annotation { "Feature Type Name" : "Feature", "Feature Type Description" : "" }
export const myFeature = defineFeature(function(context is Context, id is Id, definition is map)
    precondition{}
    {
        {
            var Q0;
            Q0=qCreatedBy(makeId("Front.planeOp"),FACE);
            var sketch = newSketch(context, id + "F0", { "sketchPlane" : qUnion([Q0])});
            skLineSegment(sketch, "E0", {"start": v(-50.37, 46.05) * mm, "end": v(25.9, 46.05) * mm});
            skLineSegment(sketch, "E1", {"start": v(25.9, 46.05) * mm, "end": v(25.9, -68.5) * mm});
            skLineSegment(sketch, "E2", {"start": v(25.9, -68.5) * mm, "end": v(-50.08, -68.5) * mm});
            skLineSegment(sketch, "E3", {"start": v(-50.08, -68.5) * mm, "end": v(-50.37, 46.05) * mm});
            skSolve(sketch);
        }
        {
            var Q0;
            Q0 = qSketchRegion(id + "F0", true);
            extrude(context, id + "F1", {"entities" : qUnion([Q0]), "depth" : 3.17 * mm});
        }
        {
            var Q0;
            Q0=makeQuery(id+"F1.opExtrude","CAP_FACE",FACE,{"disambiguationData":[OSD([sQuery(id+"F0.wireOp",EDGE,"E0"),sQuery(id+"F0.wireOp",EDGE,"E1"),sQuery(id+"F0.wireOp",EDGE,"E2"),sQuery(id+"F0.wireOp",EDGE,"E3")])],"isStart":false});
            var sketch = newSketch(context, id + "F2", { "sketchPlane" : qUnion([Q0])});
            skLineSegment(sketch, "E4", {"start": v(-31.14, 16.84) * mm, "end": v(-36.1, 15.38) * mm});
            skLineSegment(sketch, "E5", {"start": v(-36.1, 15.38) * mm, "end": v(-37.74, 17.03) * mm});
            skLineSegment(sketch, "E6", {"start": v(-37.74, 17.03) * mm, "end": v(-40.22, 17.03) * mm});
            skLineSegment(sketch, "E7", {"start": v(-40.22, 17.03) * mm, "end": v(-40.58, 17.03) * mm});
            skLineSegment(sketch, "E8", {"start": v(-40.58, 17.03) * mm, "end": v(-41.4, 15.93) * mm});
            skLineSegment(sketch, "E9", {"start": v(-41.4, 15.93) * mm, "end": v(-40.22, 15.03) * mm});
            skLineSegment(sketch, "E10", {"start": v(-40.33, 15.03) * mm, "end": v(-40.22, 15.03) * mm});
            skLineSegment(sketch, "E11", {"start": v(-40.33, 15.03) * mm, "end": v(-35.26, 13.62) * mm});
            skLineSegment(sketch, "E12", {"start": v(-35.26, 13.62) * mm, "end": v(-32.91, 12.55) * mm});
            skLineSegment(sketch, "E13", {"start": v(-32.91, 12.55) * mm, "end": v(-31.46, 11.23) * mm});
            skLineSegment(sketch, "E14", {"start": v(-31.46, 11.23) * mm, "end": v(-30.6, 8.92) * mm});
            skLineSegment(sketch, "E15", {"start": v(-30.6, 8.92) * mm, "end": v(-30.6, 6.47) * mm});
            skLineSegment(sketch, "E16", {"start": v(-30.6, 6.47) * mm, "end": v(-32.05, 4.3) * mm});
            skLineSegment(sketch, "E17", {"start": v(-32.05, 4.3) * mm, "end": v(-34.45, 2.44) * mm});
            skLineSegment(sketch, "E18", {"start": v(-34.45, 2.44) * mm, "end": v(-37.17, 1.8) * mm});
            skLineSegment(sketch, "E19", {"start": v(-37.17, 1.8) * mm, "end": v(-41.4, 1.8) * mm});
            skLineSegment(sketch, "E20", {"start": v(-41.4, 1.8) * mm, "end": v(-44.33, 2.7) * mm});
            skLineSegment(sketch, "E21", {"start": v(-44.33, 2.7) * mm, "end": v(-46.5, 4.34) * mm});
            skLineSegment(sketch, "E22", {"start": v(-46.5, 4.34) * mm, "end": v(-47.61, 6.19) * mm});
            skLineSegment(sketch, "E23", {"start": v(-47.61, 6.19) * mm, "end": v(-48.03, 7.19) * mm});
            skLineSegment(sketch, "E24", {"start": v(-48.03, 7.19) * mm, "end": v(-42.53, 8.2) * mm});
            skLineSegment(sketch, "E25", {"start": v(-42.53, 8.2) * mm, "end": v(-41.68, 7.01) * mm});
            skLineSegment(sketch, "E26", {"start": v(-41.68, 7.01) * mm, "end": v(-40.55, 6.32) * mm});
            skLineSegment(sketch, "E27", {"start": v(-40.55, 6.32) * mm, "end": v(-37.98, 6.32) * mm});
            skLineSegment(sketch, "E28", {"start": v(-37.98, 6.32) * mm, "end": v(-36.8, 6.69) * mm});
            skLineSegment(sketch, "E29", {"start": v(-36.8, 6.69) * mm, "end": v(-36.8, 7.66) * mm});
            skLineSegment(sketch, "E30", {"start": v(-36.8, 7.66) * mm, "end": v(-37.17, 8.34) * mm});
            skLineSegment(sketch, "E31", {"start": v(-37.17, 8.34) * mm, "end": v(-38.37, 8.73) * mm});
            skLineSegment(sketch, "E32", {"start": v(-38.37, 8.73) * mm, "end": v(-40.83, 9.23) * mm});
            skLineSegment(sketch, "E33", {"start": v(-40.83, 9.23) * mm, "end": v(-43.3, 9.95) * mm});
            skLineSegment(sketch, "E34", {"start": v(-43.3, 9.95) * mm, "end": v(-45.11, 10.93) * mm});
            skLineSegment(sketch, "E35", {"start": v(-45.11, 10.93) * mm, "end": v(-46.5, 12.51) * mm});
            skLineSegment(sketch, "E36", {"start": v(-46.5, 12.51) * mm, "end": v(-46.87, 13.9) * mm});
            skLineSegment(sketch, "E37", {"start": v(-46.87, 13.9) * mm, "end": v(-46.87, 15.38) * mm});
            skLineSegment(sketch, "E38", {"start": v(-46.87, 15.38) * mm, "end": v(-46.88, 17.03) * mm});
            skLineSegment(sketch, "E39", {"start": v(-46.88, 17.03) * mm, "end": v(-46.02, 18.57) * mm});
            skLineSegment(sketch, "E40", {"start": v(-46.02, 18.57) * mm, "end": v(-44.61, 20.07) * mm});
            skLineSegment(sketch, "E41", {"start": v(-44.61, 20.07) * mm, "end": v(-42.6, 21.17) * mm});
            skLineSegment(sketch, "E42", {"start": v(-42.6, 21.17) * mm, "end": v(-40.51, 21.54) * mm});
            skLineSegment(sketch, "E43", {"start": v(-40.51, 21.54) * mm, "end": v(-37.17, 21.54) * mm});
            skLineSegment(sketch, "E44", {"start": v(-37.17, 21.54) * mm, "end": v(-35.26, 21.04) * mm});
            skLineSegment(sketch, "E45", {"start": v(-35.26, 21.04) * mm, "end": v(-33.17, 19.89) * mm});
            skLineSegment(sketch, "E46", {"start": v(-33.17, 19.89) * mm, "end": v(-31.88, 18.39) * mm});
            skLineSegment(sketch, "E47", {"start": v(-31.88, 18.39) * mm, "end": v(-31.14, 16.84) * mm});
            skLineSegment(sketch, "E48", {"start": v(-29.85, 21.2) * mm, "end": v(-29.85, 16.84) * mm});
            skLineSegment(sketch, "E49", {"start": v(-29.85, 16.84) * mm, "end": v(-25.95, 16.84) * mm});
            skLineSegment(sketch, "E50", {"start": v(-25.95, 16.84) * mm, "end": v(-25.95, 2.18) * mm});
            skLineSegment(sketch, "E51", {"start": v(-25.95, 2.18) * mm, "end": v(-20.08, 2.18) * mm});
            skLineSegment(sketch, "E52", {"start": v(-20.08, 2.18) * mm, "end": v(-20.08, 16.84) * mm});
            skLineSegment(sketch, "E53", {"start": v(-20.08, 16.84) * mm, "end": v(-16.16, 16.84) * mm});
            skLineSegment(sketch, "E54", {"start": v(-16.16, 16.84) * mm, "end": v(-16.16, 21.26) * mm});
            skLineSegment(sketch, "E55", {"start": v(-16.16, 21.26) * mm, "end": v(-29.85, 21.2) * mm});
            skLineSegment(sketch, "E56", {"start": v(-14.65, 21.2) * mm, "end": v(-14.65, 2.18) * mm});
            skLineSegment(sketch, "E57", {"start": v(-14.65, 2.18) * mm, "end": v(0, 2.18) * mm});
            skLineSegment(sketch, "E58", {"start": v(0, 2.18) * mm, "end": v(0, 6.19) * mm});
            skLineSegment(sketch, "E59", {"start": v(0, 6.19) * mm, "end": v(-8.9, 6.19) * mm});
            skLineSegment(sketch, "E60", {"start": v(-8.9, 6.19) * mm, "end": v(-8.9, 9.7) * mm});
            skLineSegment(sketch, "E61", {"start": v(-8.9, 9.7) * mm, "end": v(-1.76, 9.7) * mm});
            skLineSegment(sketch, "E62", {"start": v(-1.76, 9.7) * mm, "end": v(-1.76, 14.12) * mm});
            skLineSegment(sketch, "E63", {"start": v(-1.76, 14.12) * mm, "end": v(-8.96, 14.12) * mm});
            skLineSegment(sketch, "E64", {"start": v(-8.96, 14.12) * mm, "end": v(-8.96, 16.84) * mm});
            skLineSegment(sketch, "E65", {"start": v(-8.96, 16.84) * mm, "end": v(0, 16.84) * mm});
            skLineSegment(sketch, "E66", {"start": v(0, 16.84) * mm, "end": v(0, 21.2) * mm});
            skLineSegment(sketch, "E67", {"start": v(0, 21.2) * mm, "end": v(-14.65, 21.2) * mm});
            skLineSegment(sketch, "E68", {"start": v(2.17, 21.2) * mm, "end": v(2.17, 2.01) * mm});
            skLineSegment(sketch, "E69", {"start": v(2.17, 2.01) * mm, "end": v(6.89, 2.01) * mm});
            skLineSegment(sketch, "E70", {"start": v(6.89, 2.01) * mm, "end": v(6.89, 15.02) * mm});
            skLineSegment(sketch, "E71", {"start": v(6.89, 15.02) * mm, "end": v(10.46, 1.95) * mm});
            skLineSegment(sketch, "E72", {"start": v(10.46, 1.95) * mm, "end": v(14.27, 1.95) * mm});
            skLineSegment(sketch, "E73", {"start": v(14.27, 1.95) * mm, "end": v(17.66, 15.2) * mm});
            skLineSegment(sketch, "E74", {"start": v(17.66, 15.2) * mm, "end": v(17.66, 1.83) * mm});
            skLineSegment(sketch, "E75", {"start": v(17.66, 1.83) * mm, "end": v(23.34, 1.83) * mm});
            skLineSegment(sketch, "E76", {"start": v(23.34, 1.83) * mm, "end": v(23.34, 21.2) * mm});
            skLineSegment(sketch, "E77", {"start": v(23.34, 21.2) * mm, "end": v(15.54, 21.2) * mm});
            skLineSegment(sketch, "E78", {"start": v(15.54, 21.2) * mm, "end": v(13, 11.57) * mm});
            skLineSegment(sketch, "E79", {"start": v(13, 11.57) * mm, "end": v(10.1, 21.2) * mm});
            skLineSegment(sketch, "E80", {"start": v(10.1, 21.2) * mm, "end": v(2.17, 21.2) * mm});
            skSolve(sketch);
        }
        {
            var Q0;
            Q0 = qSketchRegion(id + "F2", true);
            extrude(context, id + "F3", {"entities" : qUnion([Q0]), "operationType" : NewBodyOperationType.ADD, "depth" : 3.17 * mm});
        }
        {
            var Q0;
            Q0=makeQuery(id+"F1.opExtrude","CAP_FACE",FACE,{"disambiguationData":[OSD([sQuery(id+"F0.wireOp",EDGE,"E0"),sQuery(id+"F0.wireOp",EDGE,"E1"),sQuery(id+"F0.wireOp",EDGE,"E2"),sQuery(id+"F0.wireOp",EDGE,"E3")])],"isStart":false});
            var sketch = newSketch(context, id + "F4", { "sketchPlane" : qUnion([Q0])});
            skCircle(sketch, "E81", {"center": v(-13.1, 39.3) * mm, "radius": 3.65 * mm});
            skSolve(sketch);
        }
        {
            var Q0;
            Q0 = qSketchRegion(id + "F4", true);
            extrude(context, id + "F5", {"entities" : qUnion([Q0]), "operationType" : NewBodyOperationType.REMOVE, "oppositeDirection" : true, "depth" : 3.17 * mm});
        }
        {
            var Q0;
            Q0=makeQuery(id+"F1.opExtrude","CAP_FACE",FACE,{"disambiguationData":[OSD([sQuery(id+"F0.wireOp",EDGE,"E0"),sQuery(id+"F0.wireOp",EDGE,"E1"),sQuery(id+"F0.wireOp",EDGE,"E2"),sQuery(id+"F0.wireOp",EDGE,"E3")])],"isStart":false});
            var sketch = newSketch(context, id + "F6", { "sketchPlane" : qUnion([Q0])});
            skLineSegment(sketch, "E82", {"start": v(-41.83, -27.74) * mm, "end": v(-41.83, -28.28) * mm});
            skLineSegment(sketch, "E83", {"start": v(-41.83, -28.28) * mm, "end": v(-40.54, -28.73) * mm});
            skLineSegment(sketch, "E84", {"start": v(-40.54, -28.73) * mm, "end": v(-40.42, -35.14) * mm});
            skLineSegment(sketch, "E85", {"start": v(-40.42, -35.14) * mm, "end": v(-41.75, -35.75) * mm});
            skLineSegment(sketch, "E86", {"start": v(-41.75, -35.75) * mm, "end": v(-41.75, -36.27) * mm});
            skLineSegment(sketch, "E87", {"start": v(-41.75, -36.27) * mm, "end": v(-36.9, -36.27) * mm});
            skLineSegment(sketch, "E88", {"start": v(-36.9, -36.27) * mm, "end": v(-36.9, -35.75) * mm});
            skLineSegment(sketch, "E89", {"start": v(-36.9, -35.75) * mm, "end": v(-38, -35.32) * mm});
            skLineSegment(sketch, "E90", {"start": v(-38, -35.32) * mm, "end": v(-38, -32.36) * mm});
            skLineSegment(sketch, "E91", {"start": v(-38, -32.36) * mm, "end": v(-34.97, -36.12) * mm});
            skLineSegment(sketch, "E92", {"start": v(-34.97, -36.12) * mm, "end": v(-31.44, -36.24) * mm});
            skLineSegment(sketch, "E93", {"start": v(-31.44, -36.24) * mm, "end": v(-31.29, -35.75) * mm});
            skLineSegment(sketch, "E94", {"start": v(-31.29, -35.75) * mm, "end": v(-31.78, -35.74) * mm});
            skLineSegment(sketch, "E95", {"start": v(-31.78, -35.74) * mm, "end": v(-32.16, -35.52) * mm});
            skLineSegment(sketch, "E96", {"start": v(-32.16, -35.52) * mm, "end": v(-35.54, -32.08) * mm});
            skLineSegment(sketch, "E97", {"start": v(-35.54, -32.08) * mm, "end": v(-34.88, -31.86) * mm});
            skLineSegment(sketch, "E98", {"start": v(-34.88, -31.86) * mm, "end": v(-34.31, -31.4) * mm});
            skLineSegment(sketch, "E99", {"start": v(-34.31, -31.4) * mm, "end": v(-33.76, -30.87) * mm});
            skLineSegment(sketch, "E100", {"start": v(-33.76, -30.87) * mm, "end": v(-33.4, -30.07) * mm});
            skLineSegment(sketch, "E101", {"start": v(-33.4, -30.07) * mm, "end": v(-33.36, -29.25) * mm});
            skLineSegment(sketch, "E102", {"start": v(-33.36, -29.25) * mm, "end": v(-33.36, -28.73) * mm});
            skLineSegment(sketch, "E103", {"start": v(-33.36, -28.73) * mm, "end": v(-33.87, -28.34) * mm});
            skLineSegment(sketch, "E104", {"start": v(-33.87, -28.34) * mm, "end": v(-34.83, -27.77) * mm});
            skLineSegment(sketch, "E105", {"start": v(-34.83, -27.77) * mm, "end": v(-36.43, -27.5) * mm});
            skLineSegment(sketch, "E106", {"start": v(-36.43, -27.5) * mm, "end": v(-41.62, -27.5) * mm});
            skLineSegment(sketch, "E107", {"start": v(-41.62, -27.5) * mm, "end": v(-41.83, -27.5) * mm});
            skLineSegment(sketch, "E108", {"start": v(-41.83, -27.5) * mm, "end": v(-41.83, -27.74) * mm});
            skLineSegment(sketch, "E109", {"start": v(-38.26, -28.2) * mm, "end": v(-38.26, -31.44) * mm});
            skLineSegment(sketch, "E110", {"start": v(-38.26, -31.44) * mm, "end": v(-38.04, -31.61) * mm});
            skLineSegment(sketch, "E111", {"start": v(-38.04, -31.61) * mm, "end": v(-37.21, -31.44) * mm});
            skLineSegment(sketch, "E112", {"start": v(-37.21, -31.44) * mm, "end": v(-36.5, -30.94) * mm});
            skLineSegment(sketch, "E113", {"start": v(-36.5, -30.94) * mm, "end": v(-36.13, -30.4) * mm});
            skLineSegment(sketch, "E114", {"start": v(-36.13, -30.4) * mm, "end": v(-36.13, -29.81) * mm});
            skLineSegment(sketch, "E115", {"start": v(-36.13, -29.81) * mm, "end": v(-36.13, -29.16) * mm});
            skLineSegment(sketch, "E116", {"start": v(-36.13, -29.16) * mm, "end": v(-36.37, -28.73) * mm});
            skLineSegment(sketch, "E117", {"start": v(-36.37, -28.73) * mm, "end": v(-36.95, -28.36) * mm});
            skLineSegment(sketch, "E118", {"start": v(-36.95, -28.36) * mm, "end": v(-37.67, -28.18) * mm});
            skLineSegment(sketch, "E119", {"start": v(-37.67, -28.18) * mm, "end": v(-38.26, -28.2) * mm});
            skLineSegment(sketch, "E120", {"start": v(-27.32, -32.37) * mm, "end": v(-27.64, -31.1) * mm});
            skLineSegment(sketch, "E121", {"start": v(-27.64, -31.1) * mm, "end": v(-27.82, -30.75) * mm});
            skLineSegment(sketch, "E122", {"start": v(-27.82, -30.75) * mm, "end": v(-28.05, -30.66) * mm});
            skLineSegment(sketch, "E123", {"start": v(-28.05, -30.66) * mm, "end": v(-28.33, -30.66) * mm});
            skLineSegment(sketch, "E124", {"start": v(-28.33, -30.66) * mm, "end": v(-28.66, -30.8) * mm});
            skLineSegment(sketch, "E125", {"start": v(-28.66, -30.8) * mm, "end": v(-28.95, -31.11) * mm});
            skLineSegment(sketch, "E126", {"start": v(-28.95, -31.11) * mm, "end": v(-29.16, -31.66) * mm});
            skLineSegment(sketch, "E127", {"start": v(-29.16, -31.66) * mm, "end": v(-29.23, -32.46) * mm});
            skLineSegment(sketch, "E128", {"start": v(-29.23, -32.46) * mm, "end": v(-27.32, -32.37) * mm});
            skLineSegment(sketch, "E129", {"start": v(-24.94, -33.17) * mm, "end": v(-24.94, -32.53) * mm});
            skLineSegment(sketch, "E130", {"start": v(-24.94, -32.53) * mm, "end": v(-25.27, -31.66) * mm});
            skLineSegment(sketch, "E131", {"start": v(-25.27, -31.66) * mm, "end": v(-25.6, -31.05) * mm});
            skLineSegment(sketch, "E132", {"start": v(-25.6, -31.05) * mm, "end": v(-26.56, -30.34) * mm});
            skLineSegment(sketch, "E133", {"start": v(-26.56, -30.34) * mm, "end": v(-27.98, -29.93) * mm});
            skLineSegment(sketch, "E134", {"start": v(-27.98, -29.93) * mm, "end": v(-28.86, -29.93) * mm});
            skLineSegment(sketch, "E135", {"start": v(-28.86, -29.93) * mm, "end": v(-29.65, -30.29) * mm});
            skLineSegment(sketch, "E136", {"start": v(-29.65, -30.29) * mm, "end": v(-30.78, -31.22) * mm});
            skLineSegment(sketch, "E137", {"start": v(-30.78, -31.22) * mm, "end": v(-31.3, -32.18) * mm});
            skLineSegment(sketch, "E138", {"start": v(-31.3, -32.18) * mm, "end": v(-31.3, -32.68) * mm});
            skLineSegment(sketch, "E139", {"start": v(-31.3, -32.68) * mm, "end": v(-31.3, -34.6) * mm});
            skLineSegment(sketch, "E140", {"start": v(-31.3, -34.6) * mm, "end": v(-30.68, -35.6) * mm});
            skLineSegment(sketch, "E141", {"start": v(-30.68, -35.6) * mm, "end": v(-29.27, -36.5) * mm});
            skLineSegment(sketch, "E142", {"start": v(-29.27, -36.5) * mm, "end": v(-26.97, -36.5) * mm});
            skLineSegment(sketch, "E143", {"start": v(-26.97, -36.5) * mm, "end": v(-25.5, -35.6) * mm});
            skLineSegment(sketch, "E144", {"start": v(-25.5, -35.6) * mm, "end": v(-24.83, -34.85) * mm});
            skLineSegment(sketch, "E145", {"start": v(-24.83, -34.85) * mm, "end": v(-25.22, -34.5) * mm});
            skLineSegment(sketch, "E146", {"start": v(-25.22, -34.5) * mm, "end": v(-25.87, -35.22) * mm});
            skLineSegment(sketch, "E147", {"start": v(-25.87, -35.22) * mm, "end": v(-27.43, -35.6) * mm});
            skLineSegment(sketch, "E148", {"start": v(-27.43, -35.6) * mm, "end": v(-28.62, -35.15) * mm});
            skLineSegment(sketch, "E149", {"start": v(-28.62, -35.15) * mm, "end": v(-29.28, -34.26) * mm});
            skLineSegment(sketch, "E150", {"start": v(-29.28, -34.26) * mm, "end": v(-29.28, -33.15) * mm});
            skLineSegment(sketch, "E151", {"start": v(-29.28, -33.15) * mm, "end": v(-24.94, -33.17) * mm});
            skLineSegment(sketch, "E152", {"start": v(-18.59, -34.42) * mm, "end": v(-18.1, -34.75) * mm});
            skLineSegment(sketch, "E153", {"start": v(-18.1, -34.75) * mm, "end": v(-18.65, -35.57) * mm});
            skLineSegment(sketch, "E154", {"start": v(-18.65, -35.57) * mm, "end": v(-20.04, -36.4) * mm});
            skLineSegment(sketch, "E155", {"start": v(-20.04, -36.4) * mm, "end": v(-22.5, -36.4) * mm});
            skLineSegment(sketch, "E156", {"start": v(-22.5, -36.4) * mm, "end": v(-23.81, -35.25) * mm});
            skLineSegment(sketch, "E157", {"start": v(-23.81, -35.25) * mm, "end": v(-24.2, -34.7) * mm});
            skLineSegment(sketch, "E158", {"start": v(-24.2, -34.7) * mm, "end": v(-24.4, -34.23) * mm});
            skLineSegment(sketch, "E159", {"start": v(-24.4, -34.23) * mm, "end": v(-24.4, -33.25) * mm});
            skLineSegment(sketch, "E160", {"start": v(-24.4, -33.25) * mm, "end": v(-24, -32.01) * mm});
            skLineSegment(sketch, "E161", {"start": v(-24, -32.01) * mm, "end": v(-23.08, -30.81) * mm});
            skLineSegment(sketch, "E162", {"start": v(-23.08, -30.81) * mm, "end": v(-21.67, -30.18) * mm});
            skLineSegment(sketch, "E163", {"start": v(-21.67, -30.18) * mm, "end": v(-21.14, -29.93) * mm});
            skLineSegment(sketch, "E164", {"start": v(-21.14, -29.93) * mm, "end": v(-20.16, -29.93) * mm});
            skLineSegment(sketch, "E165", {"start": v(-20.16, -29.93) * mm, "end": v(-19.14, -30.44) * mm});
            skLineSegment(sketch, "E166", {"start": v(-19.14, -30.44) * mm, "end": v(-18.62, -30.76) * mm});
            skLineSegment(sketch, "E167", {"start": v(-18.62, -30.76) * mm, "end": v(-18.37, -31.15) * mm});
            skLineSegment(sketch, "E168", {"start": v(-18.37, -31.15) * mm, "end": v(-18.37, -31.83) * mm});
            skLineSegment(sketch, "E169", {"start": v(-18.37, -31.83) * mm, "end": v(-18.63, -32.27) * mm});
            skLineSegment(sketch, "E170", {"start": v(-18.63, -32.27) * mm, "end": v(-19.07, -32.62) * mm});
            skLineSegment(sketch, "E171", {"start": v(-19.07, -32.62) * mm, "end": v(-19.63, -32.62) * mm});
            skLineSegment(sketch, "E172", {"start": v(-19.63, -32.62) * mm, "end": v(-20.23, -32.34) * mm});
            skLineSegment(sketch, "E173", {"start": v(-20.23, -32.34) * mm, "end": v(-20.55, -32.03) * mm});
            skLineSegment(sketch, "E174", {"start": v(-20.55, -32.03) * mm, "end": v(-20.55, -31.54) * mm});
            skLineSegment(sketch, "E175", {"start": v(-20.55, -31.54) * mm, "end": v(-20.3, -31.01) * mm});
            skLineSegment(sketch, "E176", {"start": v(-20.3, -31.01) * mm, "end": v(-20.3, -30.78) * mm});
            skLineSegment(sketch, "E177", {"start": v(-20.3, -30.78) * mm, "end": v(-20.89, -30.67) * mm});
            skLineSegment(sketch, "E178", {"start": v(-20.89, -30.67) * mm, "end": v(-21.42, -30.82) * mm});
            skLineSegment(sketch, "E179", {"start": v(-21.42, -30.82) * mm, "end": v(-22.02, -31.55) * mm});
            skLineSegment(sketch, "E180", {"start": v(-22.02, -31.55) * mm, "end": v(-22.31, -32.52) * mm});
            skLineSegment(sketch, "E181", {"start": v(-22.31, -32.52) * mm, "end": v(-22.31, -33.84) * mm});
            skLineSegment(sketch, "E182", {"start": v(-22.31, -33.84) * mm, "end": v(-21.44, -35.14) * mm});
            skLineSegment(sketch, "E183", {"start": v(-21.44, -35.14) * mm, "end": v(-20.37, -35.45) * mm});
            skLineSegment(sketch, "E184", {"start": v(-20.37, -35.45) * mm, "end": v(-19.58, -35.45) * mm});
            skLineSegment(sketch, "E185", {"start": v(-19.58, -35.45) * mm, "end": v(-18.93, -34.92) * mm});
            skLineSegment(sketch, "E186", {"start": v(-15.88, -37.9) * mm, "end": v(-15.88, -37.67) * mm});
            skLineSegment(sketch, "E187", {"start": v(-15.88, -37.67) * mm, "end": v(-16.3, -37.2) * mm});
            skLineSegment(sketch, "E188", {"start": v(-16.3, -37.2) * mm, "end": v(-16.77, -36.96) * mm});
            skLineSegment(sketch, "E189", {"start": v(-16.77, -36.96) * mm, "end": v(-17.29, -36.96) * mm});
            skLineSegment(sketch, "E190", {"start": v(-17.29, -36.96) * mm, "end": v(-17.96, -37.39) * mm});
            skLineSegment(sketch, "E191", {"start": v(-17.96, -37.39) * mm, "end": v(-18.24, -37.78) * mm});
            skLineSegment(sketch, "E192", {"start": v(-18.24, -37.78) * mm, "end": v(-18.24, -38.34) * mm});
            skLineSegment(sketch, "E193", {"start": v(-18.24, -38.34) * mm, "end": v(-17.76, -38.88) * mm});
            skLineSegment(sketch, "E194", {"start": v(-17.76, -38.88) * mm, "end": v(-17.4, -39.17) * mm});
            skLineSegment(sketch, "E195", {"start": v(-17.4, -39.17) * mm, "end": v(-16.4, -39.17) * mm});
            skLineSegment(sketch, "E196", {"start": v(-16.4, -39.17) * mm, "end": v(-15.55, -38.64) * mm});
            skLineSegment(sketch, "E197", {"start": v(-15.55, -38.64) * mm, "end": v(-15.11, -38.3) * mm});
            skLineSegment(sketch, "E198", {"start": v(-15.11, -38.3) * mm, "end": v(-14.13, -36.27) * mm});
            skLineSegment(sketch, "E199", {"start": v(-14.13, -36.27) * mm, "end": v(-11.5, -30.83) * mm});
            skLineSegment(sketch, "E200", {"start": v(-11.5, -30.83) * mm, "end": v(-10.93, -30.57) * mm});
            skLineSegment(sketch, "E201", {"start": v(-10.93, -30.57) * mm, "end": v(-10.93, -30.25) * mm});
            skLineSegment(sketch, "E202", {"start": v(-10.93, -30.25) * mm, "end": v(-13.58, -30.25) * mm});
            skLineSegment(sketch, "E203", {"start": v(-13.58, -30.25) * mm, "end": v(-13.58, -30.78) * mm});
            skLineSegment(sketch, "E204", {"start": v(-13.58, -30.78) * mm, "end": v(-13.58, -31.04) * mm});
            skLineSegment(sketch, "E205", {"start": v(-13.58, -31.04) * mm, "end": v(-12.8, -31.04) * mm});
            skLineSegment(sketch, "E206", {"start": v(-12.8, -31.04) * mm, "end": v(-12.54, -31.04) * mm});
            skLineSegment(sketch, "E207", {"start": v(-12.54, -31.04) * mm, "end": v(-13.97, -34.32) * mm});
            skLineSegment(sketch, "E208", {"start": v(-13.97, -34.32) * mm, "end": v(-15.6, -31.08) * mm});
            skLineSegment(sketch, "E209", {"start": v(-15.6, -31.08) * mm, "end": v(-14.91, -30.4) * mm});
            skLineSegment(sketch, "E210", {"start": v(-14.91, -30.4) * mm, "end": v(-16.47, -30.4) * mm});
            skLineSegment(sketch, "E211", {"start": v(-16.47, -30.4) * mm, "end": v(-18.53, -30.4) * mm});
            skLineSegment(sketch, "E212", {"start": v(-18.53, -30.4) * mm, "end": v(-18.26, -31.1) * mm});
            skLineSegment(sketch, "E213", {"start": v(-18.26, -31.1) * mm, "end": v(-17.86, -31.1) * mm});
            skLineSegment(sketch, "E214", {"start": v(-17.86, -31.1) * mm, "end": v(-15.92, -34.49) * mm});
            skLineSegment(sketch, "E215", {"start": v(-15.92, -34.49) * mm, "end": v(-14.86, -36.37) * mm});
            skLineSegment(sketch, "E216", {"start": v(-10.54, -33.8) * mm, "end": v(-10.1, -34.97) * mm});
            skLineSegment(sketch, "E217", {"start": v(-10.1, -34.97) * mm, "end": v(-9.21, -36.02) * mm});
            skLineSegment(sketch, "E218", {"start": v(-9.21, -36.02) * mm, "end": v(-7.8, -36.42) * mm});
            skLineSegment(sketch, "E219", {"start": v(-7.8, -36.42) * mm, "end": v(-6.52, -36.42) * mm});
            skLineSegment(sketch, "E220", {"start": v(-6.52, -36.42) * mm, "end": v(-5.74, -36.17) * mm});
            skLineSegment(sketch, "E221", {"start": v(-5.74, -36.17) * mm, "end": v(-4.75, -35.48) * mm});
            skLineSegment(sketch, "E222", {"start": v(-4.75, -35.48) * mm, "end": v(-4.08, -34.65) * mm});
            skLineSegment(sketch, "E223", {"start": v(-4.08, -34.65) * mm, "end": v(-4.42, -34.38) * mm});
            skPoint(sketch, "E223.endSnap0", {"position": v(-4.42, -35.07) * mm});
            skLineSegment(sketch, "E224", {"start": v(-4.42, -34.38) * mm, "end": v(-5.48, -35.26) * mm});
            skLineSegment(sketch, "E225", {"start": v(-5.48, -35.26) * mm, "end": v(-6.35, -35.52) * mm});
            skLineSegment(sketch, "E226", {"start": v(-6.35, -35.52) * mm, "end": v(-7.32, -35.24) * mm});
            skLineSegment(sketch, "E227", {"start": v(-7.32, -35.24) * mm, "end": v(-7.77, -34.84) * mm});
            skLineSegment(sketch, "E228", {"start": v(-7.77, -34.84) * mm, "end": v(-8.35, -33.86) * mm});
            skLineSegment(sketch, "E229", {"start": v(-8.35, -33.86) * mm, "end": v(-8.35, -32.16) * mm});
            skLineSegment(sketch, "E230", {"start": v(-8.35, -32.16) * mm, "end": v(-7.87, -31.19) * mm});
            skLineSegment(sketch, "E231", {"start": v(-7.87, -31.19) * mm, "end": v(-7.17, -30.68) * mm});
            skLineSegment(sketch, "E232", {"start": v(-7.17, -30.68) * mm, "end": v(-6.38, -30.68) * mm});
            skLineSegment(sketch, "E233", {"start": v(-6.38, -30.68) * mm, "end": v(-6.08, -31) * mm});
            skLineSegment(sketch, "E234", {"start": v(-6.08, -31) * mm, "end": v(-6.48, -31) * mm});
            skLineSegment(sketch, "E235", {"start": v(-6.48, -31) * mm, "end": v(-6.74, -31.78) * mm});
            skLineSegment(sketch, "E236", {"start": v(-6.74, -31.78) * mm, "end": v(-6.44, -32.59) * mm});
            skLineSegment(sketch, "E237", {"start": v(-6.44, -32.59) * mm, "end": v(-5.41, -32.9) * mm});
            skLineSegment(sketch, "E238", {"start": v(-5.41, -32.9) * mm, "end": v(-4.66, -32.42) * mm});
            skLineSegment(sketch, "E239", {"start": v(-4.66, -32.42) * mm, "end": v(-4.66, -31.45) * mm});
            skLineSegment(sketch, "E240", {"start": v(-4.66, -31.45) * mm, "end": v(-4.66, -30.82) * mm});
            skLineSegment(sketch, "E241", {"start": v(-4.66, -30.82) * mm, "end": v(-5.51, -30.27) * mm});
            skLineSegment(sketch, "E242", {"start": v(-5.51, -30.27) * mm, "end": v(-6.55, -29.91) * mm});
            skLineSegment(sketch, "E243", {"start": v(-6.55, -29.91) * mm, "end": v(-7.52, -29.91) * mm});
            skPoint(sketch, "E243.endSnap0", {"position": v(-7.52, -30.93) * mm});
            skLineSegment(sketch, "E244", {"start": v(-7.52, -29.91) * mm, "end": v(-8.78, -30.45) * mm});
            skLineSegment(sketch, "E245", {"start": v(-8.78, -30.45) * mm, "end": v(-9.88, -31.4) * mm});
            skLineSegment(sketch, "E246", {"start": v(-9.88, -31.4) * mm, "end": v(-10.54, -32.5) * mm});
            skLineSegment(sketch, "E247", {"start": v(-10.54, -32.5) * mm, "end": v(-10.54, -33.8) * mm});
            skLineSegment(sketch, "E248", {"start": v(-3.53, -27.77) * mm, "end": v(-4.66, -27.77) * mm});
            skLineSegment(sketch, "E249", {"start": v(-4.66, -27.77) * mm, "end": v(-4.66, -26.8) * mm});
            skLineSegment(sketch, "E250", {"start": v(-4.66, -26.8) * mm, "end": v(-1.43, -26.8) * mm});
            skLineSegment(sketch, "E251", {"start": v(-1.43, -26.8) * mm, "end": v(-1.43, -35.44) * mm});
            skLineSegment(sketch, "E252", {"start": v(-1.43, -35.44) * mm, "end": v(-0.36, -35.82) * mm});
            skLineSegment(sketch, "E253", {"start": v(-0.36, -35.82) * mm, "end": v(-0.36, -36.4) * mm});
            skLineSegment(sketch, "E254", {"start": v(-0.36, -36.4) * mm, "end": v(-4.51, -36.4) * mm});
            skLineSegment(sketch, "E255", {"start": v(-4.51, -36.4) * mm, "end": v(-4.42, -35.9) * mm});
            skLineSegment(sketch, "E256", {"start": v(-4.42, -35.9) * mm, "end": v(-3.44, -35.44) * mm});
            skLineSegment(sketch, "E257", {"start": v(-3.44, -35.44) * mm, "end": v(-3.44, -33.2) * mm});
            skLineSegment(sketch, "E258", {"start": v(-3.44, -33.2) * mm, "end": v(-3.53, -27.77) * mm});
            skLineSegment(sketch, "E259", {"start": v(2.54, -30) * mm, "end": v(2.54, -35.48) * mm});
            skLineSegment(sketch, "E260", {"start": v(2.54, -35.48) * mm, "end": v(3.64, -35.92) * mm});
            skLineSegment(sketch, "E261", {"start": v(3.64, -35.92) * mm, "end": v(3.64, -36.24) * mm});
            skLineSegment(sketch, "E262", {"start": v(3.64, -36.24) * mm, "end": v(0, -36.24) * mm});
            skLineSegment(sketch, "E263", {"start": v(0, -36.24) * mm, "end": v(-0.36, -36.11) * mm});
            skLineSegment(sketch, "E264", {"start": v(-0.36, -36.11) * mm, "end": v(-0.36, -35.82) * mm});
            skLineSegment(sketch, "E265", {"start": v(0, -35.7) * mm, "end": v(-0.36, -35.82) * mm});
            skLineSegment(sketch, "E266", {"start": v(0.44, -35.64) * mm, "end": v(0, -35.7) * mm});
            skLineSegment(sketch, "E267", {"start": v(0.44, -35.64) * mm, "end": v(0.44, -31.16) * mm});
            skLineSegment(sketch, "E268", {"start": v(0.44, -31.16) * mm, "end": v(-0.8, -30.8) * mm});
            skLineSegment(sketch, "E269", {"start": v(-0.8, -30.8) * mm, "end": v(-0.65, -30.28) * mm});
            skLineSegment(sketch, "E270", {"start": v(-0.65, -30.28) * mm, "end": v(1.86, -30.16) * mm});
            skLineSegment(sketch, "E271", {"start": v(1.86, -30.16) * mm, "end": v(2.54, -30) * mm});
            skLineSegment(sketch, "E272", {"start": v(4.44, -30.95) * mm, "end": v(4.44, -35.81) * mm});
            skLineSegment(sketch, "E273", {"start": v(4.44, -35.81) * mm, "end": v(3.64, -35.92) * mm});
            skLineSegment(sketch, "E274", {"start": v(3.62, -36.34) * mm, "end": v(7.34, -36.34) * mm});
            skLineSegment(sketch, "E275", {"start": v(7.34, -36.34) * mm, "end": v(7.34, -35.78) * mm});
            skLineSegment(sketch, "E276", {"start": v(7.34, -35.78) * mm, "end": v(6.4, -35.78) * mm});
            skLineSegment(sketch, "E277", {"start": v(6.4, -35.78) * mm, "end": v(6.4, -31.87) * mm});
            skLineSegment(sketch, "E278", {"start": v(6.4, -31.87) * mm, "end": v(7.24, -31.33) * mm});
            skLineSegment(sketch, "E279", {"start": v(7.24, -31.33) * mm, "end": v(7.94, -31.33) * mm});
            skLineSegment(sketch, "E280", {"start": v(7.94, -31.33) * mm, "end": v(8.8, -31.89) * mm});
            skLineSegment(sketch, "E281", {"start": v(8.8, -31.89) * mm, "end": v(8.8, -35.76) * mm});
            skLineSegment(sketch, "E282", {"start": v(8.8, -35.76) * mm, "end": v(8.05, -35.76) * mm});
            skLineSegment(sketch, "E283", {"start": v(8.05, -35.76) * mm, "end": v(8.05, -36.38) * mm});
            skLineSegment(sketch, "E284", {"start": v(8.05, -36.38) * mm, "end": v(11.97, -36.38) * mm});
            skLineSegment(sketch, "E285", {"start": v(11.97, -36.38) * mm, "end": v(11.97, -35.73) * mm});
            skLineSegment(sketch, "E286", {"start": v(11.97, -35.73) * mm, "end": v(10.95, -35.73) * mm});
            skLineSegment(sketch, "E287", {"start": v(10.95, -35.73) * mm, "end": v(10.95, -31.26) * mm});
            skLineSegment(sketch, "E288", {"start": v(10.95, -31.26) * mm, "end": v(10.08, -30.21) * mm});
            skLineSegment(sketch, "E289", {"start": v(10.08, -30.21) * mm, "end": v(8.8, -30.21) * mm});
            skLineSegment(sketch, "E290", {"start": v(8.8, -30.21) * mm, "end": v(8, -30.21) * mm});
            skLineSegment(sketch, "E291", {"start": v(8, -30.21) * mm, "end": v(6.66, -30.93) * mm});
            skLineSegment(sketch, "E292", {"start": v(6.66, -30.93) * mm, "end": v(6.66, -30.07) * mm});
            skLineSegment(sketch, "E293", {"start": v(6.66, -30.07) * mm, "end": v(3.4, -30.07) * mm});
            skLineSegment(sketch, "E294", {"start": v(3.4, -30.07) * mm, "end": v(3.4, -30.84) * mm});
            skLineSegment(sketch, "E295", {"start": v(3.64, -36.24) * mm, "end": v(7.34, -36.34) * mm});
            skLineSegment(sketch, "E296", {"start": v(19.01, -30.28) * mm, "end": v(18.92, -31.1) * mm});
            skLineSegment(sketch, "E297", {"start": v(18.92, -31.1) * mm, "end": v(17.66, -31.06) * mm});
            skLineSegment(sketch, "E298", {"start": v(17.66, -31.06) * mm, "end": v(18, -32.19) * mm});
            skLineSegment(sketch, "E299", {"start": v(18, -32.19) * mm, "end": v(17.5, -32.93) * mm});
            skLineSegment(sketch, "E300", {"start": v(17.5, -32.93) * mm, "end": v(16.92, -33.58) * mm});
            skLineSegment(sketch, "E301", {"start": v(16.92, -33.58) * mm, "end": v(15.32, -34.13) * mm});
            skLineSegment(sketch, "E302", {"start": v(15.32, -34.13) * mm, "end": v(14.32, -34.13) * mm});
            skLineSegment(sketch, "E303", {"start": v(14.32, -34.13) * mm, "end": v(13.77, -34.48) * mm});
            skLineSegment(sketch, "E304", {"start": v(13.77, -34.48) * mm, "end": v(14, -34.84) * mm});
            skLineSegment(sketch, "E305", {"start": v(14, -34.84) * mm, "end": v(17.66, -34.84) * mm});
            skLineSegment(sketch, "E306", {"start": v(17.66, -34.84) * mm, "end": v(18.48, -35.5) * mm});
            skLineSegment(sketch, "E307", {"start": v(18.48, -35.5) * mm, "end": v(18.87, -36.56) * mm});
            skLineSegment(sketch, "E308", {"start": v(18.87, -36.56) * mm, "end": v(18.65, -37.85) * mm});
            skLineSegment(sketch, "E309", {"start": v(18.65, -37.85) * mm, "end": v(16.83, -38.91) * mm});
            skLineSegment(sketch, "E310", {"start": v(16.83, -38.91) * mm, "end": v(13.28, -38.91) * mm});
            skLineSegment(sketch, "E311", {"start": v(13.28, -38.91) * mm, "end": v(12.7, -38.91) * mm});
            skLineSegment(sketch, "E312", {"start": v(12.7, -38.91) * mm, "end": v(12.1, -38.56) * mm});
            skLineSegment(sketch, "E313", {"start": v(12.1, -38.56) * mm, "end": v(11.8, -38.1) * mm});
            skLineSegment(sketch, "E314", {"start": v(11.8, -38.1) * mm, "end": v(11.8, -37.53) * mm});
            skLineSegment(sketch, "E315", {"start": v(11.8, -37.53) * mm, "end": v(11.98, -36.96) * mm});
            skLineSegment(sketch, "E316", {"start": v(11.98, -36.96) * mm, "end": v(13.4, -36.39) * mm});
            skLineSegment(sketch, "E317", {"start": v(13.4, -36.39) * mm, "end": v(12.6, -35.73) * mm});
            skLineSegment(sketch, "E318", {"start": v(12.6, -35.73) * mm, "end": v(12.25, -34.94) * mm});
            skLineSegment(sketch, "E319", {"start": v(12.25, -34.94) * mm, "end": v(13.02, -34.32) * mm});
            skLineSegment(sketch, "E320", {"start": v(13.02, -34.32) * mm, "end": v(13.77, -34.07) * mm});
            skLineSegment(sketch, "E321", {"start": v(13.77, -34.07) * mm, "end": v(12.53, -33.42) * mm});
            skLineSegment(sketch, "E322", {"start": v(12.53, -33.42) * mm, "end": v(12.07, -32.68) * mm});
            skLineSegment(sketch, "E323", {"start": v(12.07, -32.68) * mm, "end": v(12.07, -31.82) * mm});
            skLineSegment(sketch, "E324", {"start": v(12.07, -31.82) * mm, "end": v(12.18, -31.08) * mm});
            skLineSegment(sketch, "E325", {"start": v(12.18, -31.08) * mm, "end": v(13.18, -30.37) * mm});
            skLineSegment(sketch, "E326", {"start": v(13.18, -30.37) * mm, "end": v(14.4, -30.09) * mm});
            skLineSegment(sketch, "E327", {"start": v(14.4, -30.09) * mm, "end": v(15.7, -30.15) * mm});
            skLineSegment(sketch, "E328", {"start": v(15.7, -30.15) * mm, "end": v(16.21, -30.49) * mm});
            skLineSegment(sketch, "E329", {"start": v(16.21, -30.49) * mm, "end": v(19.01, -30.28) * mm});
            skLineSegment(sketch, "E330", {"start": v(14.91, -30.67) * mm, "end": v(15.44, -31.03) * mm});
            skLineSegment(sketch, "E331", {"start": v(15.44, -31.03) * mm, "end": v(15.85, -31.37) * mm});
            skLineSegment(sketch, "E332", {"start": v(15.85, -31.37) * mm, "end": v(15.32, -33.53) * mm});
            skLineSegment(sketch, "E333", {"start": v(15.32, -33.53) * mm, "end": v(14.83, -33.53) * mm});
            skLineSegment(sketch, "E334", {"start": v(14.83, -33.53) * mm, "end": v(14.32, -33.17) * mm});
            skLineSegment(sketch, "E335", {"start": v(14.32, -33.17) * mm, "end": v(14.32, -31.32) * mm});
            skLineSegment(sketch, "E336", {"start": v(14.32, -31.32) * mm, "end": v(14.44, -30.86) * mm});
            skLineSegment(sketch, "E337", {"start": v(14.44, -30.86) * mm, "end": v(14.91, -30.67) * mm});
            skLineSegment(sketch, "E338", {"start": v(16.62, -36.87) * mm, "end": v(16.62, -38.14) * mm});
            skLineSegment(sketch, "E339", {"start": v(16.62, -38.14) * mm, "end": v(15.76, -38.56) * mm});
            skLineSegment(sketch, "E340", {"start": v(15.76, -38.56) * mm, "end": v(14.64, -38.67) * mm});
            skLineSegment(sketch, "E341", {"start": v(14.64, -38.67) * mm, "end": v(13.78, -37.75) * mm});
            skLineSegment(sketch, "E342", {"start": v(13.78, -37.75) * mm, "end": v(13.94, -36.71) * mm});
            skLineSegment(sketch, "E343", {"start": v(16.62, -36.87) * mm, "end": v(13.94, -36.71) * mm});
            skCircle(sketch, "E344", {"center": v(0.97, -28) * mm, "radius": 1.2 * mm});
            skLineSegment(sketch, "E345", {"start": v(-18.93, -34.92) * mm, "end": v(-18.59, -34.42) * mm});
            skLineSegment(sketch, "E346", {"start": v(-14.86, -36.37) * mm, "end": v(-15.88, -37.9) * mm});
            skLineSegment(sketch, "E347", {"start": v(3.4, -30.84) * mm, "end": v(4.44, -30.95) * mm});
            skSolve(sketch);
        }
        {
            var Q0;
            Q0=makeQuery(id+"F6.imprint","IMPRINT",FACE,{"disambiguationData":[TD([[makeQuery(id+"F6.imprint","IMPRINT",EDGE,{"derivedFrom":sQuery(id+"F6.wireOp",EDGE,"E82")}),-1.0]])]});
            var sketch = newSketch(context, id + "F7", { "sketchPlane" : qUnion([Q0])});
            skText(sketch, "E348", { "text": "HALL PASS", "fontName": "RobotoSlab-Regular.ttf"});
            const initialGuessF7  = {"E348": [-0.04976, -0.0594, 1, 0, 0.0096]};
            skSetInitialGuess(sketch, initialGuessF7);
            skSolve(sketch);
        }
        {
            var Q0;
            Q0 = qSketchRegion(id + "F7", true);
            extrude(context, id + "F8", {"entities" : qUnion([Q0]), "operationType" : NewBodyOperationType.REMOVE, "oppositeDirection" : true, "depth" : 3.17 * mm});
        }
        {
            var Q0;
            Q0 = qSketchRegion(id + "F6", true);
            extrude(context, id + "F9", {"entities" : qUnion([Q0]), "operationType" : NewBodyOperationType.REMOVE, "oppositeDirection" : true, "depth" : 3.17 * mm});
        }
        {
            var Q0;
            Q0=makeQuery(id+"F6.imprint","IMPRINT",FACE,{"disambiguationData":[TD([[makeQuery(id+"F6.imprint","IMPRINT",EDGE,{"derivedFrom":sQuery(id+"F6.wireOp",EDGE,"E82")}),-1.0]])]});
            var sketch = newSketch(context, id + "F10", { "sketchPlane" : qUnion([Q0])});
            skLineSegment(sketch, "E349", {"start": v(-14.16, -14.54) * mm, "end": v(-14.16, -20.25) * mm});
            skLineSegment(sketch, "E350", {"start": v(-14.16, -20.25) * mm, "end": v(-19.33, -20.25) * mm});
            skLineSegment(sketch, "E351", {"start": v(-19.33, -20.25) * mm, "end": v(-22.84, -14.21) * mm});
            skLineSegment(sketch, "E352", {"start": v(-22.84, -14.21) * mm, "end": v(-22.84, -13.24) * mm});
            skLineSegment(sketch, "E353", {"start": v(-22.84, -13.24) * mm, "end": v(-21, -9.9) * mm});
            skLineSegment(sketch, "E354", {"start": v(-21, -9.9) * mm, "end": v(-21.93, -9.4) * mm});
            skLineSegment(sketch, "E355", {"start": v(-21.93, -9.4) * mm, "end": v(-17.12, -8.72) * mm});
            skLineSegment(sketch, "E356", {"start": v(-17.12, -8.72) * mm, "end": v(-15.13, -13.35) * mm});
            skLineSegment(sketch, "E357", {"start": v(-15.13, -13.35) * mm, "end": v(-16.05, -12.92) * mm});
            skLineSegment(sketch, "E358", {"start": v(-16.05, -12.92) * mm, "end": v(-17.1, -14.51) * mm});
            skLineSegment(sketch, "E359", {"start": v(-17.1, -14.51) * mm, "end": v(-14.16, -14.54) * mm});
            skLineSegment(sketch, "E360", {"start": v(-10.71, -13.42) * mm, "end": v(-10.71, -14.54) * mm});
            skLineSegment(sketch, "E361", {"start": v(-10.71, -14.54) * mm, "end": v(-8.76, -14.54) * mm});
            skLineSegment(sketch, "E362", {"start": v(-8.76, -14.54) * mm, "end": v(-10.2, -11.95) * mm});
            skLineSegment(sketch, "E363", {"start": v(-10.2, -11.95) * mm, "end": v(-5.27, -9.24) * mm});
            skLineSegment(sketch, "E364", {"start": v(-5.27, -9.24) * mm, "end": v(-2.78, -13.3) * mm});
            skLineSegment(sketch, "E365", {"start": v(-2.78, -13.3) * mm, "end": v(-2.78, -13.97) * mm});
            skLineSegment(sketch, "E366", {"start": v(-2.78, -13.97) * mm, "end": v(-6.31, -20.02) * mm});
            skLineSegment(sketch, "E367", {"start": v(-6.31, -20.02) * mm, "end": v(-10.67, -20.02) * mm});
            skLineSegment(sketch, "E368", {"start": v(-10.67, -20.02) * mm, "end": v(-10.67, -21.27) * mm});
            skLineSegment(sketch, "E369", {"start": v(-10.67, -21.27) * mm, "end": v(-13.68, -17.43) * mm});
            skLineSegment(sketch, "E370", {"start": v(-13.68, -17.43) * mm, "end": v(-10.71, -13.42) * mm});
            skLineSegment(sketch, "E371", {"start": v(-14.16, -9.9) * mm, "end": v(-12.84, -7.37) * mm});
            skLineSegment(sketch, "E372", {"start": v(-12.84, -7.37) * mm, "end": v(-11.87, -8.99) * mm});
            skLineSegment(sketch, "E373", {"start": v(-11.87, -8.99) * mm, "end": v(-12.73, -9.5) * mm});
            skLineSegment(sketch, "E374", {"start": v(-12.73, -9.5) * mm, "end": v(-8.12, -10.24) * mm});
            skLineSegment(sketch, "E375", {"start": v(-8.12, -10.24) * mm, "end": v(-5.9, -5.51) * mm});
            skLineSegment(sketch, "E376", {"start": v(-5.9, -5.51) * mm, "end": v(-6.94, -6.1) * mm});
            skLineSegment(sketch, "E377", {"start": v(-6.94, -6.1) * mm, "end": v(-8.72, -2.88) * mm});
            skLineSegment(sketch, "E378", {"start": v(-8.72, -2.88) * mm, "end": v(-9.61, -2.44) * mm});
            skLineSegment(sketch, "E379", {"start": v(-9.61, -2.44) * mm, "end": v(-16.28, -2.44) * mm});
            skLineSegment(sketch, "E380", {"start": v(-16.28, -2.44) * mm, "end": v(-19.34, -7.2) * mm});
            skLineSegment(sketch, "E381", {"start": v(-19.34, -7.2) * mm, "end": v(-14.16, -9.9) * mm});
            skSolve(sketch);
        }
        {
            var Q0;
            Q0 = qSketchRegion(id + "F10", true);
            extrude(context, id + "F11", {"entities" : qUnion([Q0]), "operationType" : NewBodyOperationType.REMOVE, "oppositeDirection" : true, "depth" : 3.17 * mm});
        }
    });